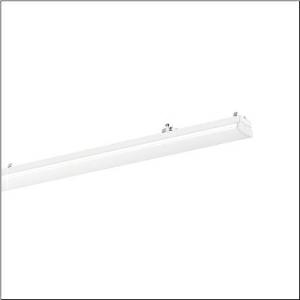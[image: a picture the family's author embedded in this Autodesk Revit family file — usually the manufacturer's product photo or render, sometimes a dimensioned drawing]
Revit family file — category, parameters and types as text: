
# Revit family: licross_r__21_recessed_opal_mo_52te1ddn495g_a365
name_source: partatom
category: Lighting Fixtures
units: mm (PartAtom-declared; Revit-internal decimal feet)

## family parameters
Cut with Voids When Loaded = No
Host = Face
Light Source = No
Part Type = Normal
Room Calculation Point = No
Round Connector Dimension = Use Diameter
Shared = No

## types (1)
- --- (1 x LED, 9740 lm, 58 W, 4000K)
    Apparent Load = 58 VA
    CIE Flux Codes = 44 73 91 87 100
    Color Rendering = 80
    Color Temperature = 4000K
    Default Elevation = 1800 mm
    Description = Licross® 21 recessed opal MO, luminaire insert, of sheet steel, galvanised, coil coated, white, length: 1.500mm, width: 66mm, height: 67mm, LED rated luminous flux: 9.750lm, light colour: 840, control gear: DALI 2, with plug, 5-pole, with phase selection, mains connection: 220..240V, AC, 50/60Hz, rated input power: 58W, internal wiring halogen-free, primary optical cover: cover, of PMMA, light emission: direct with ceiling illumination distribution, primary light characteristic: symmetric, protection rating (complete): IP54, insulation class (complete): insulation class I (protective earthing), certification: CE, ENEC, VDE, UKCA, protection symbol: D if used in an environment with non-conductive dust loads with corresponding accessories, impact resistance: IK06, permissible ambient temperature for indoor applications: -25..+35°C, corresponds to IFS (International Featured Standards) requirements for safety and quality in the food industry, reducing of maximum allowable ambient temperature of 5°C with ceiling mounting, LABS conformity tested according to VDMA 24364:2018-05, packaging unit: 1 piece
    Height = 83 mm
    Lamp = 1 x LED
    Lamp Light Flux = 9740 lm
    Lamp Power = 58 W
    Lamp count = 1
    Length = 1500 mm
    Luminous efficacy = 168 lm/W
    Manufacturer = Siteco
    ModVariant = No
    Model = 52TE1DDN495G
    Mounting Place = Ceiling
    Mounting Type = Pendant
    Number of Poles = 1
    OnlyDefault = Yes
    Power Factor = 1
    Product Name = Licross® 21 recessed opal MO
    Product group = luminaire insert | ceiling pendant
    ProductGroupID = 902
    Protection Class = Protection class I
    Protection Degree = IP 54
    RLX_Detail_Level = 1
    RLX_Emergency_Light_Flux = 0 lm
    RLX_Emergency_Type = 0
    RLX_Emergency_Type_DB = No
    RlxData = <blob elided: 27185 chars, md5=067c35d2>
    Socket = socket
    Standby Power = 0 W
    System Light Flux = 9740 lm
    System Power = 58 W
    Type Comments = factory setting: luminous flux: 100 % | dim-lin: 254 | 390 mA
    Type Image = l_1313666.jpg
    URL = http://relux.com
    VarID = @adj_090027
    Voltage = 0 V
    Weight = 0.00 kg
    Width = 76 mm

## geometry (parser evidence)
native form markers: Blend x4, Sweep x12
no freeform markers — native parametric forms only
